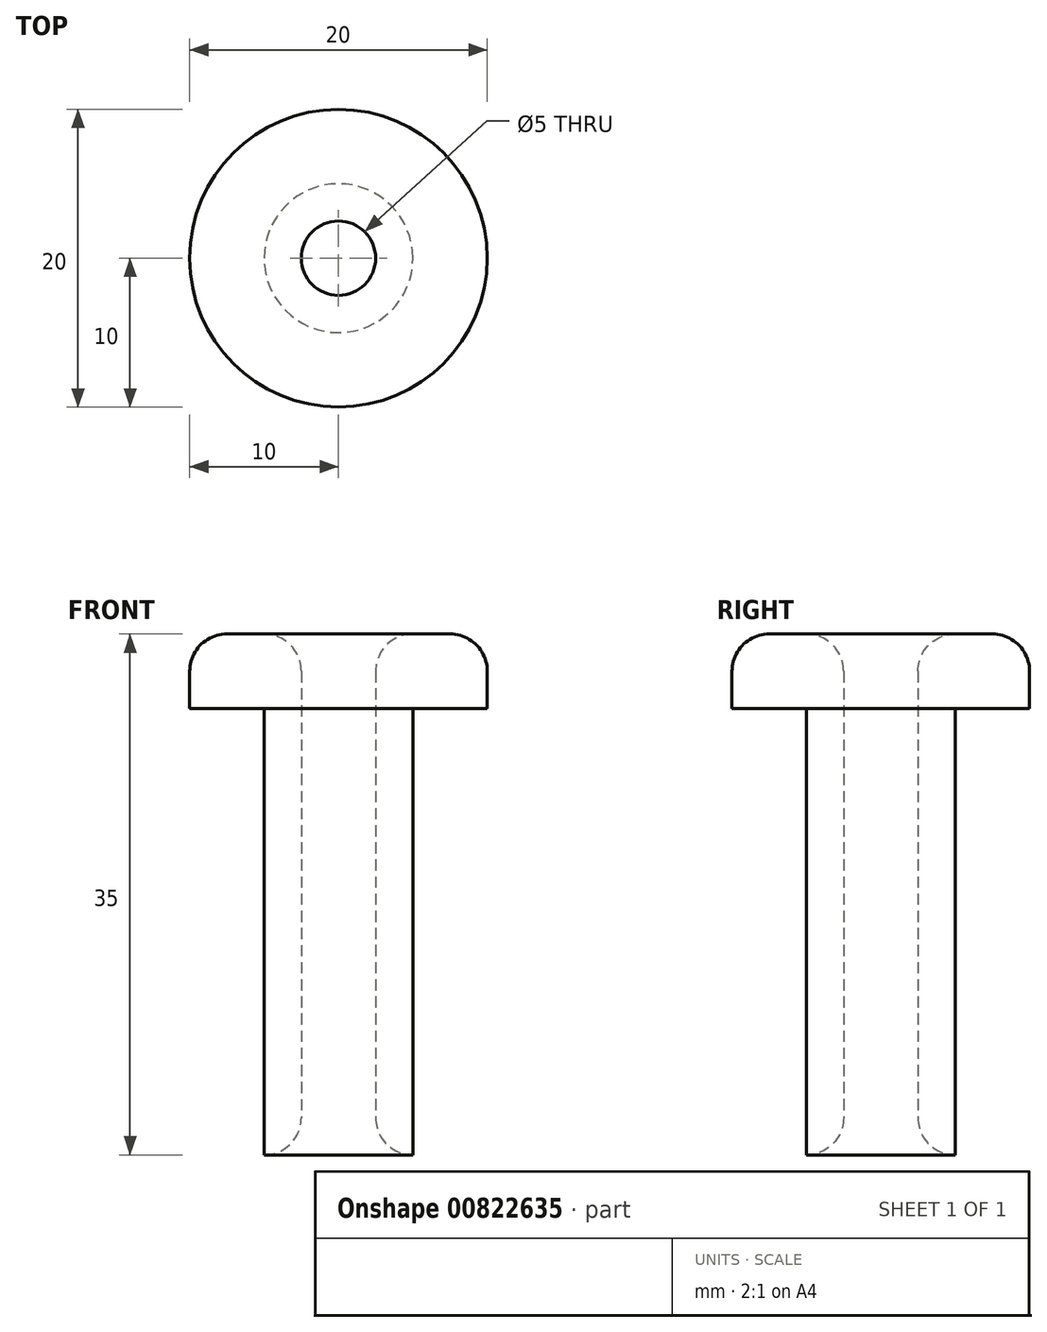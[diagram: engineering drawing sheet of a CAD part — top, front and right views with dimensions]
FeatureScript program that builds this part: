
annotation { "Feature Type Name" : "Feature", "Feature Type Description" : "" }
export const myFeature = defineFeature(function(context is Context, id is Id, definition is map)
    precondition{}
    {
        {
            var Q0;
            Q0=qCreatedBy(makeId("Top.planeOp"),FACE);
            var sketch = newSketch(context, id + "F0", { "sketchPlane" : qUnion([Q0])});
            skCircle(sketch, "E0", {"center": v(0, 0) * mm, "radius": 10 * mm});
            skCircle(sketch, "E1", {"center": v(0, 0) * mm, "radius": 2.5 * mm});
            skSolve(sketch);
        }
        {
            var Q0;
            Q0 = qSketchRegion(id + "F0", true);
            extrude(context, id + "F1", {"entities" : qUnion([Q0]), "depth" : 5 * mm, "offsetDistance" : 25 * mm});
        }
        {
            var Q0;
            Q0=makeQuery(id+"F1.opExtrude","CAP_FACE",FACE,{"disambiguationData":[OSD([sQuery(id+"F0.wireOp",EDGE,"E0"),sQuery(id+"F0.wireOp",EDGE,"E1")])],"isStart":true});
            var sketch = newSketch(context, id + "F2", { "sketchPlane" : qUnion([Q0])});
            skCircle(sketch, "E2", {"center": v(0, 0) * mm, "radius": 5 * mm});
            skCircle(sketch, "E3", {"center": v(0, 0) * mm, "radius": 2.5 * mm});
            skSolve(sketch);
        }
        {
            var Q0;
            Q0 = qSketchRegion(id + "F2", true);
            extrude(context, id + "F3", {"entities" : qUnion([Q0]), "operationType" : NewBodyOperationType.ADD, "depth" : 30 * mm, "offsetDistance" : 25 * mm});
        }
        {
            var Q0;
            Q0=makeQuery(id+"F1.opExtrude","CAP_EDGE",EDGE,{"disambiguationData":[OSD([sQuery(id+"F0.wireOp",EDGE,"E0")])],"isStart":false});
            var Q1;
            Q1=makeQuery(id+"F1.opExtrude","CAP_EDGE",EDGE,{"disambiguationData":[OSD([sQuery(id+"F0.wireOp",EDGE,"E1")])],"isStart":false});
            var Q2;
            Q2=makeQuery(id+"F3.opExtrude","CAP_EDGE",EDGE,{"disambiguationData":[OSD([sQuery(id+"F2.wireOp",EDGE,"E3")])],"isStart":false});
            fillet(context, id + "F4", {"entities" : qUnion([Q0, Q1, Q2]), "radius" : 2.5 * mm, "tangentPropagation" : true, "allowEdgeOverflow" : false});
        }
    });
